# Revit family: S-tank_P2
name_source: partatom
category: Оборудование
units: mm (PartAtom-declared; Revit-internal decimal feet)

## family parameters
Всегда вертикально = Да
Классификация = Нет
На основе рабочей плоскости = Нет
Общий = Нет
При загрузке вырезать с полостями = Нет
Размер круглого соединителя = Использовать диаметр
Тип детали = Нормальный
Точка расчета площади = Нет

## types (8) — shared parameters
ADSK_URL документации изделия = http://s-tank.ru
ADSK_Группирование = Оборудование
ADSK_Единица измерения = шт.
ADSK_Завод-изготовитель = ООО “С-ТЭНК ВОТЕР ХИТЕРС”
ADSK_Наименование = Бойлер косвенного нагрева
DN1 = 25 мм
DN2 = 15 мм
shrf = 18 мм
Разработка семейств = https://rubim.tech

## per-type parameters (varying)
| type | A | ADSK_Масса | B | C | D | E | G | H | J | K | L | M | N | a | Диаметрcизоляцией |
| P2 200 | 198 мм | 58 | 308 мм | 438 мм | 508 мм | 618 мм | 198 мм | 1200 мм | 1020 мм | 728 мм | 888 мм | 958 мм | 1038 мм | 96 мм | 575 мм |
| P2 300 | 198 мм | 70 | 318 мм | 538 мм | 608 мм | 728 мм | 198 мм | 1550 мм | 1360 мм | 888 мм | 1168 мм | 1238 мм | 1318 мм | 96 мм | 575 мм |
| P2 400 | 210 мм | 85 | 340 мм | 420 мм | 590 мм | 720 мм | 210 мм | 1420 мм | 1110 мм | 850 мм | 950 мм | 1030 мм | 1100 мм | 121 мм | 725 мм |
| P2 500 | 210 мм | 93 | 340 мм | 420 мм | 590 мм | 720 мм | 210 мм | 1670 мм | 1360 мм | 850 мм | 1000 мм | 1080 мм | 1150 мм | 121 мм | 725 мм |
| P2 750 | 286 мм | 114 | 416 мм | 496 мм | 606 мм | 736 мм | 286 мм | 1630 мм | 1326 мм | 866 мм | 1016 мм | 1096 мм | 1166 мм | 153 мм | 920 мм |
| P2 1000 | 296 мм | 145 | 486 мм | 581 мм | 696 мм | 886 мм | 296 мм | 2200 мм | 1876 мм | 1076 мм | 1211 мм | 1306 мм | 1361 мм | 153 мм | 920 мм |
| P2 1500 | 360 мм | 211 | 550 мм | 645 мм | 880 мм | 1070 мм | 360 мм | 2370 мм | 2010 мм | 1260 мм | 1535 мм | 1630 мм | 1685 мм | 178 мм | 1070 мм |
| P2 2000 | 308 мм | 257 | 508 мм | 603 мм | 908 мм | 1108 мм | 508 мм | 2500 мм | 2178 мм | 1308 мм | 1633 мм | 1728 мм | 1783 мм | 197 мм | 1180 мм |

note: column(s) folded — value = type name in every type: ADSK_Марка, ADSK_Обозначение
